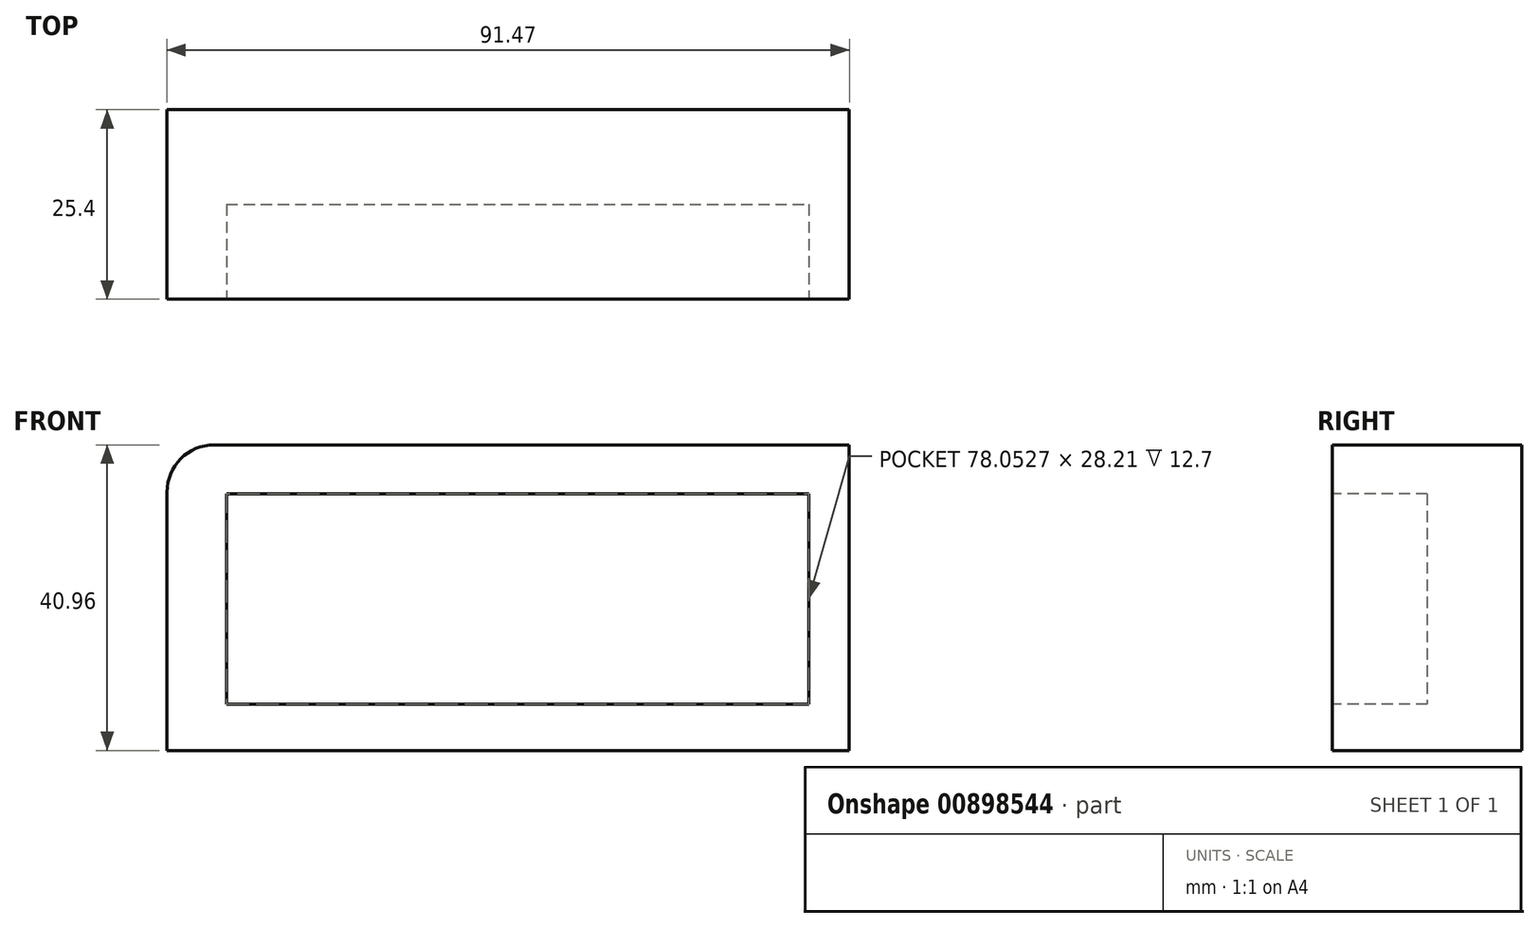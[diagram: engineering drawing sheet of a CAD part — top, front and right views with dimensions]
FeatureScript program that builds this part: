
annotation { "Feature Type Name" : "Feature", "Feature Type Description" : "" }
export const myFeature = defineFeature(function(context is Context, id is Id, definition is map)
    precondition{}
    {
        {
            var Q0;
            Q0=qCreatedBy(makeId("Front.planeOp"),FACE);
            var sketch = newSketch(context, id + "F0", { "sketchPlane" : qUnion([Q0])});
            skLineSegment(sketch, "E0.bottom", {"start": v(-33.97, 20.57) * mm, "end": v(51.15, 20.57) * mm});
            skLineSegment(sketch, "E0.top", {"start": v(-40.32, -20.39) * mm, "end": v(51.15, -20.39) * mm});
            skLineSegment(sketch, "E0.left", {"start": v(-40.32, 14.22) * mm, "end": v(-40.32, -20.39) * mm});
            skLineSegment(sketch, "E0.right", {"start": v(51.15, 20.57) * mm, "end": v(51.15, -20.39) * mm});
            skPoint(sketch, "E1.visualSharp", {"position": v(-40.32, 20.57) * mm});
            skArc(sketch, "E1.filletArc", {"start": v(-33.97, 20.57) * mm, "mid": v(-38.46, 18.7) * mm, "end": v(-40.32, 14.22) * mm});
            skSolve(sketch);
        }
        {
            var Q0;
            Q0=makeQuery(id+"F0.imprint","IMPRINT",FACE,{"disambiguationData":[TD([[makeQuery(id+"F0.imprint","IMPRINT",EDGE,{"derivedFrom":sQuery(id+"F0.wireOp",EDGE,"E0.bottom")}),-1.0]])]});
            extrude(context, id + "F1", {"entities" : qUnion([Q0]), "depth" : 25.4 * mm, "offsetDistance" : 25.4 * mm});
        }
        {
            var Q0;
            Q0=makeQuery(id+"F1.opExtrude","CAP_FACE",FACE,{"disambiguationData":[OSD([sQuery(id+"F0.wireOp",EDGE,"E0.bottom"),sQuery(id+"F0.wireOp",EDGE,"E0.top"),sQuery(id+"F0.wireOp",EDGE,"E0.left"),sQuery(id+"F0.wireOp",EDGE,"E0.right"),sQuery(id+"F0.wireOp",EDGE,"E1.filletArc")])],"isStart":false});
            var sketch = newSketch(context, id + "F2", { "sketchPlane" : qUnion([Q0])});
            skLineSegment(sketch, "E2.bottom", {"start": v(-32.34, 14) * mm, "end": v(45.71, 14) * mm});
            skLineSegment(sketch, "E2.top", {"start": v(-32.34, -14.2) * mm, "end": v(45.71, -14.2) * mm});
            skLineSegment(sketch, "E2.left", {"start": v(-32.34, 14) * mm, "end": v(-32.34, -14.2) * mm});
            skLineSegment(sketch, "E2.right", {"start": v(45.71, 14) * mm, "end": v(45.71, -14.2) * mm});
            skSolve(sketch);
        }
        {
            var Q0;
            Q0=makeQuery(id+"F2.imprint","IMPRINT",FACE,{"disambiguationData":[TD([[makeQuery(id+"F2.imprint","IMPRINT",EDGE,{"derivedFrom":sQuery(id+"F2.wireOp",EDGE,"E2.bottom")}),-1.0]])]});
            extrude(context, id + "F3", {"entities" : qUnion([Q0]), "operationType" : NewBodyOperationType.REMOVE, "oppositeDirection" : true, "depth" : 12.7 * mm, "offsetDistance" : 25.4 * mm});
        }
    });
